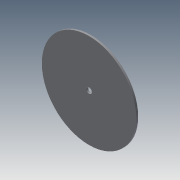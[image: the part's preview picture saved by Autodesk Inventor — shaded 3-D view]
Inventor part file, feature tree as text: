
AUTODESK INVENTOR PART (.ipt)
format: ipt  version: 2013 (Build 170138000, 138)  size: 73,216 bytes
history: native  units: mm
features: extrude x2, sketch x2
ambient origin geometry x8: Origin, YZ Plane, XZ Plane, XY Plane, X Axis, Y Axis, Z Axis, Center Point
bodies: Solid1 (feature_tree)
feature tree (4):
  extrude  "Extrusion1"  Depth=6.0mm
  extrude  "Extrusion2"  [1 undecoded]
  sketch  "Sketch1"  dims[d1=2.0mm d2=0.0mm d3=6.0mm]
  sketch  "Sketch2"  dims[d4=2.0mm d5=0.0mm]
note: 1 required parameter value undecoded (feature->parameter linkage not recoverable at this tier; creation-order binding heuristic only, values carry confidence <= 0.55)
